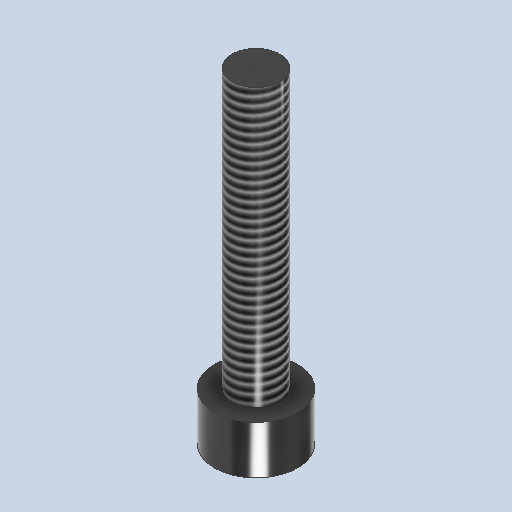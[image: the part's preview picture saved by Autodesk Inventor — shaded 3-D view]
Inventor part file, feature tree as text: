
AUTODESK INVENTOR PART (.ipt)
format: ipt  version: 2024.2 (Build 282272000, 272)  size: 166,400 bytes
history: native  units: mm
features: sketch x2, revolve x1, thread x1, extrude x1
ambient origin geometry x8: Origin, YZ Plane, XZ Plane, XY Plane, X Axis, Y Axis, Z Axis, Center Point
bodies: Solid1 (feature_tree)
feature tree (5):
  revolve  "Revolution1"  [1 undecoded]
  thread  "Thread1"  [1 undecoded]
  extrude  "Extrusion1"  [1 undecoded]
  sketch  "Sketch1"  dims[d4=90.0deg d5=6.0mm d6=0.0mm d0=0.0mm]
  sketch  "Sketch2"
note: 3 required parameter values undecoded (feature->parameter linkage not recoverable at this tier; creation-order binding heuristic only, values carry confidence <= 0.55)